# Revit family: PI-20_GENERADO
name_source: partatom
category: Equipos mecánicos
revit_build: Autodesk Revit 2014 (Build: 20130308_1515(x64)
units: mm (PartAtom-declared; Revit-internal decimal feet)

## types (6) — shared parameters
Depth = 635 mm  [stored 2.08333 ft]
Fabricante = SAMMIC S.L.
Foodservice Equipment Identifier = Sí
Height = 735 mm  [stored 2.41142 ft]
Revision Code = 1
Specification by Manufacturer = Not only to peel potatoes, but also suitable to peel carrots and other similar products.
URL = https://www.sammic.com
Weight in Pounds = 78.9
Width = 433 mm  [stored 1.4206 ft]

## per-type parameters (varying)
| type | Comentarios de tipo | Cycle | Electric Connection Type | FL Amps | Modelo | URL Cutsheet | Volts |
| Potato peeler PI-20 120/60/1 | Stainless steel construction commercial potato peeler. 20 Kg. / 44 pounds load per cycle. | 60 Hz | USA | 5 A | 1000618 | http://www.sammic.com | 120 V |
| Potato peeler PI-20  230-400/50/3N | Stainless steel construction commercial potato peeler. 20 Kg. / 44 pounds load per cycle.

ELECTRICAL DATA:

230V/50Hz/3~ (2.8A) | 50 Hz |  | 1 A | 1000660 | http://www.sammic.com | 400 V |
| Potato peeler PI-20  230/50/1 | Stainless steel construction commercial potato peeler. 20 Kg. / 44 pounds load per cycle. | 50 Hz |  | 3 A | 1000661 | http://www.sammic.com | 230 V |
| Potato peeler PI-20 220-380/60/3N | Stainless steel construction commercial potato peeler. 20 Kg. / 44 pounds load per cycle.

ELECTRICAL DATA:

380V/60Hz/3N~ (1.5A) | 60 Hz |  | 2 A | 1000662 | http://www.sammic.com | 220 V |
| Potato peeler PI-20 220/60/1 | Stainless steel construction commercial potato peeler. 20 Kg. / 44 pounds load per cycle. | 60 Hz |  | 3 A | 1000663 | http://www.sammic.com | 220 V |
| Potato peeler PI-20 220/60/1 KSA | Stainless steel construction commercial potato peeler. 20 Kg. / 44 pounds load per cycle. | 60 Hz |  | 3 A | 1000666 |  | 220 V |

note: column(s) folded — value = type name in every type: Descripción

note: [stored X ft] marks values corroborated as IEEE doubles in the binary element streams (Revit-internal decimal feet)
